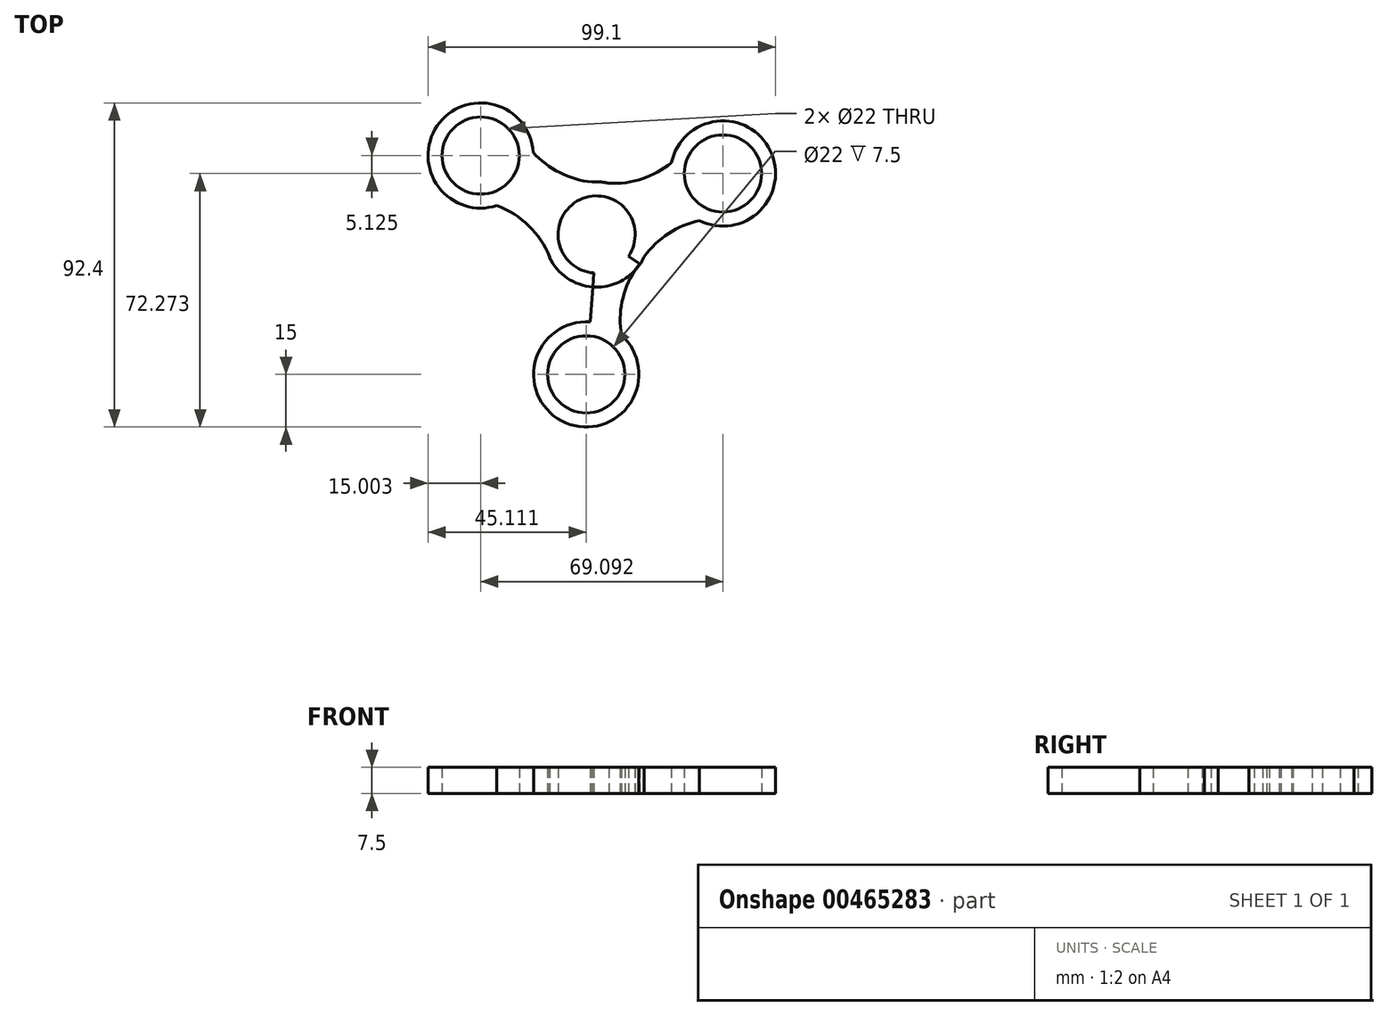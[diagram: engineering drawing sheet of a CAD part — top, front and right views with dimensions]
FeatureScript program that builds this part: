
annotation { "Feature Type Name" : "Feature", "Feature Type Description" : "" }
export const myFeature = defineFeature(function(context is Context, id is Id, definition is map)
    precondition{}
    {
        {
            var Q0;
            Q0=qCreatedBy(makeId("Top.planeOp"),FACE);
            var sketch = newSketch(context, id + "F0", { "sketchPlane" : qUnion([Q0])});
            skCircle(sketch, "E0", {"center": v(0, 0) * mm, "radius": 11 * mm});
            skCircle(sketch, "E1", {"center": v(0, 0) * mm, "radius": 15 * mm});
            skLineSegment(sketch, "E2", {"start": v(0, 0) * mm, "end": v(-33.07, 22.5) * mm});
            skLineSegment(sketch, "E3.1.0", {"start": v(0, 0) * mm, "end": v(-2.96, -39.9) * mm});
            skLineSegment(sketch, "E3.2.0", {"start": v(0, 0) * mm, "end": v(36.03, 17.38) * mm});
            skCircle(sketch, "E4", {"center": v(-33.07, 22.5) * mm, "radius": 11 * mm});
            skCircle(sketch, "E5", {"center": v(-33.07, 22.5) * mm, "radius": 15 * mm});
            skCircle(sketch, "E6", {"center": v(36.03, 17.38) * mm, "radius": 11 * mm});
            skCircle(sketch, "E7", {"center": v(36.03, 17.38) * mm, "radius": 15 * mm});
            skCircle(sketch, "E8", {"center": v(-2.96, -39.9) * mm, "radius": 11 * mm});
            skCircle(sketch, "E9", {"center": v(-2.96, -39.9) * mm, "radius": 15 * mm});
            skArc(sketch, "E10", {"start": v(0, 15) * mm, "mid": v(17.14, 17.67) * mm, "end": v(28.8, 30.52) * mm});
            skLineSegment(sketch, "E11", {"start": v(-2.96, -39.9) * mm, "end": v(3.85, 51.85) * mm});
            skLineSegment(sketch, "E12", {"start": v(-33.07, 22.5) * mm, "end": v(40.3, -27.44) * mm});
            skLineSegment(sketch, "E13", {"start": v(36.03, 17.38) * mm, "end": v(-52.53, -25.35) * mm});
            skArc(sketch, "E14.MirrorCS", {"start": v(2.21, 14.84) * mm, "mid": v(-14.35, 20) * mm, "end": v(-23.97, 34.44) * mm});
            skArc(sketch, "E15.MirrorCS", {"start": v(-13, -7.5) * mm, "mid": v(-23.87, 6.01) * mm, "end": v(-40.83, 9.67) * mm});
            skArc(sketch, "E16.MirrorCS", {"start": v(-13.95, -5.5) * mm, "mid": v(-10.15, -22.43) * mm, "end": v(-17.84, -37.98) * mm});
            skArc(sketch, "E17.MirrorCS", {"start": v(13, -7.5) * mm, "mid": v(6.73, -23.68) * mm, "end": v(12.04, -40.2) * mm});
            skArc(sketch, "E18.MirrorCS", {"start": v(11.74, -9.33) * mm, "mid": v(24.5, 2.43) * mm, "end": v(41.8, 3.54) * mm});
            skSolve(sketch);
        }
        {
            var Q0;
            {var subQ0=sQuery(id+"F0.wireOp",EDGE,"E14.MirrorCS");var subQ1=sQuery(id+"F0.wireOp",EDGE,"E1");var subQ2=makeQuery(id+"F0.imprint","INTERSECT",VERTEX,{"disambiguationData":[OD(1.0)],"derivedFrom":[subQ1,subQ0]});Q0=makeQuery(id+"F0.imprint","IMPRINT",FACE,{"disambiguationData":[TD([[makeQuery(id+"F0.imprint","IMPRINT",EDGE,{"disambiguationData":[TD([[subQ2,-1.0]])],"derivedFrom":subQ1}),-1.0]])]});}
            var Q1;
            {var subQ0=sQuery(id+"F0.wireOp",EDGE,"E13");var subQ1=sQuery(id+"F0.wireOp",EDGE,"E0");var subQ2=makeQuery(id+"F0.imprint","INTERSECT",VERTEX,{"disambiguationData":[OD(1.0)],"derivedFrom":[subQ1,subQ0]});Q1=makeQuery(id+"F0.imprint","IMPRINT",FACE,{"disambiguationData":[TD([[makeQuery(id+"F0.imprint","IMPRINT",EDGE,{"disambiguationData":[TD([[subQ2,-1.0]])],"derivedFrom":subQ1}),-1.0]])]});}
            var Q2;
            Q2=makeQuery(id+"F0.imprint","IMPRINT",FACE,{"disambiguationData":[TD([[makeQuery(id+"F0.imprint","IMPRINT",EDGE,{"derivedFrom":sQuery(id+"F0.wireOp",EDGE,"E4")}),-1.0]])]});
            var Q3;
            {var subQ0=sQuery(id+"F0.wireOp",EDGE,"E13");var subQ1=sQuery(id+"F0.wireOp",EDGE,"E0");var subQ2=makeQuery(id+"F0.imprint","INTERSECT",VERTEX,{"disambiguationData":[OD(0.0)],"derivedFrom":[subQ1,subQ0]});Q3=makeQuery(id+"F0.imprint","IMPRINT",FACE,{"disambiguationData":[TD([[makeQuery(id+"F0.imprint","IMPRINT",EDGE,{"disambiguationData":[TD([[subQ2,1.0]])],"derivedFrom":subQ1}),-1.0]])]});}
            var Q4;
            {var subQ0=sQuery(id+"F0.wireOp",EDGE,"E10");var subQ1=sQuery(id+"F0.wireOp",EDGE,"E7");var subQ2=makeQuery(id+"F0.imprint","INTERSECT",VERTEX,{"disambiguationData":[OD(0.0)],"derivedFrom":[subQ1,subQ0]});Q4=makeQuery(id+"F0.imprint","IMPRINT",FACE,{"disambiguationData":[TD([[makeQuery(id+"F0.imprint","IMPRINT",EDGE,{"disambiguationData":[TD([[subQ2,-1.0]])],"derivedFrom":subQ1}),1.0]])]});}
            var Q5;
            {var subQ0=sQuery(id+"F0.wireOp",EDGE,"E18.MirrorCS");var subQ1=sQuery(id+"F0.wireOp",EDGE,"E7");var subQ2=makeQuery(id+"F0.imprint","INTERSECT",VERTEX,{"disambiguationData":[OD(0.0)],"derivedFrom":[subQ1,subQ0]});Q5=makeQuery(id+"F0.imprint","IMPRINT",FACE,{"disambiguationData":[TD([[makeQuery(id+"F0.imprint","IMPRINT",EDGE,{"disambiguationData":[TD([[subQ2,1.0]])],"derivedFrom":subQ1}),1.0]])]});}
            var Q6;
            {var subQ0=sQuery(id+"F0.wireOp",EDGE,"E18.MirrorCS");var subQ1=sQuery(id+"F0.wireOp",EDGE,"E1");var subQ2=makeQuery(id+"F0.imprint","INTERSECT",VERTEX,{"disambiguationData":[OD(1.0)],"derivedFrom":[subQ1,subQ0]});Q6=makeQuery(id+"F0.imprint","IMPRINT",FACE,{"disambiguationData":[TD([[makeQuery(id+"F0.imprint","IMPRINT",EDGE,{"disambiguationData":[TD([[subQ2,-1.0]])],"derivedFrom":subQ1}),-1.0]])]});}
            var Q7;
            {var subQ1=sQuery(id+"F0.wireOp",EDGE,"E0");var subQ5=sQuery(id+"F0.wireOp",EDGE,"E11");var subQ6=makeQuery(id+"F0.imprint","INTERSECT",VERTEX,{"disambiguationData":[OD(1.0)],"derivedFrom":[subQ1,subQ5]});Q7=makeQuery(id+"F0.imprint","IMPRINT",FACE,{"disambiguationData":[TD([[makeQuery(id+"F0.imprint","IMPRINT",EDGE,{"disambiguationData":[TD([[subQ6,-1.0]])],"derivedFrom":subQ1}),-1.0]])]});}
            var Q8;
            {var subQ0=sQuery(id+"F0.wireOp",EDGE,"E16.MirrorCS");var subQ1=sQuery(id+"F0.wireOp",EDGE,"E1");var subQ2=makeQuery(id+"F0.imprint","INTERSECT",VERTEX,{"disambiguationData":[OD(1.0)],"derivedFrom":[subQ1,subQ0]});Q8=makeQuery(id+"F0.imprint","IMPRINT",FACE,{"disambiguationData":[TD([[makeQuery(id+"F0.imprint","IMPRINT",EDGE,{"disambiguationData":[TD([[subQ2,-1.0]])],"derivedFrom":subQ1}),-1.0]])]});}
            var Q9;
            {var subQ0=sQuery(id+"F0.wireOp",EDGE,"E10");var subQ1=sQuery(id+"F0.wireOp",EDGE,"E1");var subQ2=makeQuery(id+"F0.imprint","INTERSECT",VERTEX,{"disambiguationData":[OD(1.0)],"derivedFrom":[subQ1,subQ0]});Q9=makeQuery(id+"F0.imprint","IMPRINT",FACE,{"disambiguationData":[TD([[makeQuery(id+"F0.imprint","IMPRINT",EDGE,{"disambiguationData":[TD([[subQ2,1.0]])],"derivedFrom":subQ1}),-1.0]])]});}
            var Q10;
            {var subQ0=sQuery(id+"F0.wireOp",EDGE,"E17.MirrorCS");var subQ1=sQuery(id+"F0.wireOp",EDGE,"E9");var subQ2=makeQuery(id+"F0.imprint","INTERSECT",VERTEX,{"disambiguationData":[OD(0.0)],"derivedFrom":[subQ1,subQ0]});Q10=makeQuery(id+"F0.imprint","IMPRINT",FACE,{"disambiguationData":[TD([[makeQuery(id+"F0.imprint","IMPRINT",EDGE,{"disambiguationData":[TD([[subQ2,-1.0]])],"derivedFrom":subQ1}),1.0]])]});}
            var Q11;
            {var subQ0=sQuery(id+"F0.wireOp",EDGE,"E16.MirrorCS");var subQ1=sQuery(id+"F0.wireOp",EDGE,"E9");var subQ2=makeQuery(id+"F0.imprint","INTERSECT",VERTEX,{"disambiguationData":[OD(0.0)],"derivedFrom":[subQ1,subQ0]});Q11=makeQuery(id+"F0.imprint","IMPRINT",FACE,{"disambiguationData":[TD([[makeQuery(id+"F0.imprint","IMPRINT",EDGE,{"disambiguationData":[TD([[subQ2,1.0]])],"derivedFrom":subQ1}),1.0]])]});}
            var Q12;
            {var subQ0=sQuery(id+"F0.wireOp",EDGE,"E14.MirrorCS");var subQ1=sQuery(id+"F0.wireOp",EDGE,"E5");var subQ2=makeQuery(id+"F0.imprint","INTERSECT",VERTEX,{"disambiguationData":[OD(0.0)],"derivedFrom":[subQ1,subQ0]});Q12=makeQuery(id+"F0.imprint","IMPRINT",FACE,{"disambiguationData":[TD([[makeQuery(id+"F0.imprint","IMPRINT",EDGE,{"disambiguationData":[TD([[subQ2,1.0]])],"derivedFrom":subQ1}),1.0]])]});}
            var Q13;
            {var subQ0=sQuery(id+"F0.wireOp",EDGE,"E15.MirrorCS");var subQ1=sQuery(id+"F0.wireOp",EDGE,"E5");var subQ2=makeQuery(id+"F0.imprint","INTERSECT",VERTEX,{"disambiguationData":[OD(0.0)],"derivedFrom":[subQ1,subQ0]});Q13=makeQuery(id+"F0.imprint","IMPRINT",FACE,{"disambiguationData":[TD([[makeQuery(id+"F0.imprint","IMPRINT",EDGE,{"disambiguationData":[TD([[subQ2,-1.0]])],"derivedFrom":subQ1}),1.0]])]});}
            var Q14;
            {var subQ3=sQuery(id+"F0.wireOp",EDGE,"E11");var subQ7=sQuery(id+"F0.wireOp",EDGE,"E0");var subQ8=makeQuery(id+"F0.imprint","INTERSECT",VERTEX,{"disambiguationData":[OD(0.0)],"derivedFrom":[subQ7,subQ3]});Q14=makeQuery(id+"F0.imprint","IMPRINT",FACE,{"disambiguationData":[TD([[makeQuery(id+"F0.imprint","IMPRINT",EDGE,{"disambiguationData":[TD([[subQ8,1.0]])],"derivedFrom":subQ7}),-1.0]])]});}
            var Q15;
            {var subQ0=sQuery(id+"F0.wireOp",EDGE,"E15.MirrorCS");var subQ1=sQuery(id+"F0.wireOp",EDGE,"E1");var subQ2=makeQuery(id+"F0.imprint","INTERSECT",VERTEX,{"disambiguationData":[OD(1.0)],"derivedFrom":[subQ1,subQ0]});Q15=makeQuery(id+"F0.imprint","IMPRINT",FACE,{"disambiguationData":[TD([[makeQuery(id+"F0.imprint","IMPRINT",EDGE,{"disambiguationData":[TD([[subQ2,1.0]])],"derivedFrom":subQ1}),-1.0]])]});}
            var Q16;
            Q16=makeQuery(id+"F0.imprint","IMPRINT",FACE,{"disambiguationData":[TD([[makeQuery(id+"F0.imprint","IMPRINT",EDGE,{"derivedFrom":sQuery(id+"F0.wireOp",EDGE,"E6")}),-1.0]])]});
            var Q17;
            {var subQ0=sQuery(id+"F0.wireOp",EDGE,"E12");var subQ1=sQuery(id+"F0.wireOp",EDGE,"E0");var subQ2=makeQuery(id+"F0.imprint","INTERSECT",VERTEX,{"disambiguationData":[OD(0.0)],"derivedFrom":[subQ1,subQ0]});Q17=makeQuery(id+"F0.imprint","IMPRINT",FACE,{"disambiguationData":[TD([[makeQuery(id+"F0.imprint","IMPRINT",EDGE,{"disambiguationData":[TD([[subQ2,-1.0]])],"derivedFrom":subQ1}),-1.0]])]});}
            var Q18;
            {var subQ1=sQuery(id+"F0.wireOp",EDGE,"E0");var subQ5=sQuery(id+"F0.wireOp",EDGE,"E11");var subQ6=makeQuery(id+"F0.imprint","INTERSECT",VERTEX,{"disambiguationData":[OD(0.0)],"derivedFrom":[subQ1,subQ5]});Q18=makeQuery(id+"F0.imprint","IMPRINT",FACE,{"disambiguationData":[TD([[makeQuery(id+"F0.imprint","IMPRINT",EDGE,{"disambiguationData":[TD([[subQ6,-1.0]])],"derivedFrom":subQ1}),-1.0]])]});}
            var Q19;
            {var subQ0=sQuery(id+"F0.wireOp",EDGE,"E17.MirrorCS");var subQ1=sQuery(id+"F0.wireOp",EDGE,"E1");var subQ2=makeQuery(id+"F0.imprint","INTERSECT",VERTEX,{"disambiguationData":[OD(1.0)],"derivedFrom":[subQ1,subQ0]});Q19=makeQuery(id+"F0.imprint","IMPRINT",FACE,{"disambiguationData":[TD([[makeQuery(id+"F0.imprint","IMPRINT",EDGE,{"disambiguationData":[TD([[subQ2,1.0]])],"derivedFrom":subQ1}),-1.0]])]});}
            var Q20;
            Q20=makeQuery(id+"F0.imprint","IMPRINT",FACE,{"disambiguationData":[TD([[makeQuery(id+"F0.imprint","IMPRINT",EDGE,{"derivedFrom":sQuery(id+"F0.wireOp",EDGE,"E8")}),-1.0]])]});
            var Q21;
            {var subQ0=sQuery(id+"F0.wireOp",EDGE,"E10");var subQ1=sQuery(id+"F0.wireOp",EDGE,"E1");var subQ2=makeQuery(id+"F0.imprint","INTERSECT",VERTEX,{"disambiguationData":[OD(0.0)],"derivedFrom":[subQ1,subQ0]});Q21=makeQuery(id+"F0.imprint","IMPRINT",FACE,{"disambiguationData":[TD([[makeQuery(id+"F0.imprint","IMPRINT",EDGE,{"disambiguationData":[TD([[subQ2,1.0]])],"derivedFrom":subQ1}),1.0]])]});}
            var Q22;
            {var subQ0=sQuery(id+"F0.wireOp",EDGE,"E10");var subQ1=sQuery(id+"F0.wireOp",EDGE,"E1");var subQ2=makeQuery(id+"F0.imprint","INTERSECT",VERTEX,{"disambiguationData":[OD(0.0)],"derivedFrom":[subQ1,subQ0]});Q22=makeQuery(id+"F0.imprint","IMPRINT",FACE,{"disambiguationData":[TD([[makeQuery(id+"F0.imprint","IMPRINT",EDGE,{"disambiguationData":[TD([[subQ2,-1.0]])],"derivedFrom":subQ1}),1.0]])]});}
            var Q23;
            {var subQ0=sQuery(id+"F0.wireOp",EDGE,"E14.MirrorCS");var subQ1=sQuery(id+"F0.wireOp",EDGE,"E1");var subQ2=makeQuery(id+"F0.imprint","INTERSECT",VERTEX,{"disambiguationData":[OD(0.0)],"derivedFrom":[subQ1,subQ0]});Q23=makeQuery(id+"F0.imprint","IMPRINT",FACE,{"disambiguationData":[TD([[makeQuery(id+"F0.imprint","IMPRINT",EDGE,{"disambiguationData":[TD([[subQ2,1.0]])],"derivedFrom":subQ1}),1.0]])]});}
            var Q24;
            {var subQ0=sQuery(id+"F0.wireOp",EDGE,"E17.MirrorCS");var subQ1=sQuery(id+"F0.wireOp",EDGE,"E1");var subQ2=makeQuery(id+"F0.imprint","INTERSECT",VERTEX,{"disambiguationData":[OD(0.0)],"derivedFrom":[subQ1,subQ0]});Q24=makeQuery(id+"F0.imprint","IMPRINT",FACE,{"disambiguationData":[TD([[makeQuery(id+"F0.imprint","IMPRINT",EDGE,{"disambiguationData":[TD([[subQ2,-1.0]])],"derivedFrom":subQ1}),1.0]])]});}
            var Q25;
            {var subQ0=sQuery(id+"F0.wireOp",EDGE,"E18.MirrorCS");var subQ1=sQuery(id+"F0.wireOp",EDGE,"E1");var subQ2=makeQuery(id+"F0.imprint","INTERSECT",VERTEX,{"disambiguationData":[OD(0.0)],"derivedFrom":[subQ1,subQ0]});Q25=makeQuery(id+"F0.imprint","IMPRINT",FACE,{"disambiguationData":[TD([[makeQuery(id+"F0.imprint","IMPRINT",EDGE,{"disambiguationData":[TD([[subQ2,1.0]])],"derivedFrom":subQ1}),1.0]])]});}
            var Q26;
            {var subQ0=sQuery(id+"F0.wireOp",EDGE,"E15.MirrorCS");var subQ1=sQuery(id+"F0.wireOp",EDGE,"E1");var subQ2=makeQuery(id+"F0.imprint","INTERSECT",VERTEX,{"disambiguationData":[OD(0.0)],"derivedFrom":[subQ1,subQ0]});Q26=makeQuery(id+"F0.imprint","IMPRINT",FACE,{"disambiguationData":[TD([[makeQuery(id+"F0.imprint","IMPRINT",EDGE,{"disambiguationData":[TD([[subQ2,1.0]])],"derivedFrom":subQ1}),1.0]])]});}
            var Q27;
            {var subQ0=sQuery(id+"F0.wireOp",EDGE,"E16.MirrorCS");var subQ1=sQuery(id+"F0.wireOp",EDGE,"E1");var subQ2=makeQuery(id+"F0.imprint","INTERSECT",VERTEX,{"disambiguationData":[OD(0.0)],"derivedFrom":[subQ1,subQ0]});Q27=makeQuery(id+"F0.imprint","IMPRINT",FACE,{"disambiguationData":[TD([[makeQuery(id+"F0.imprint","IMPRINT",EDGE,{"disambiguationData":[TD([[subQ2,1.0]])],"derivedFrom":subQ1}),1.0]])]});}
            var Q28;
            {var subQ0=sQuery(id+"F0.wireOp",EDGE,"E15.MirrorCS");var subQ1=sQuery(id+"F0.wireOp",EDGE,"E1");var subQ2=makeQuery(id+"F0.imprint","INTERSECT",VERTEX,{"disambiguationData":[OD(0.0)],"derivedFrom":[subQ1,subQ0]});Q28=makeQuery(id+"F0.imprint","IMPRINT",FACE,{"disambiguationData":[TD([[makeQuery(id+"F0.imprint","IMPRINT",EDGE,{"disambiguationData":[TD([[subQ2,-1.0]])],"derivedFrom":subQ1}),1.0]])]});}
            var Q29;
            {var subQ0=sQuery(id+"F0.wireOp",EDGE,"E17.MirrorCS");var subQ1=sQuery(id+"F0.wireOp",EDGE,"E1");var subQ2=makeQuery(id+"F0.imprint","INTERSECT",VERTEX,{"disambiguationData":[OD(0.0)],"derivedFrom":[subQ1,subQ0]});Q29=makeQuery(id+"F0.imprint","IMPRINT",FACE,{"disambiguationData":[TD([[makeQuery(id+"F0.imprint","IMPRINT",EDGE,{"disambiguationData":[TD([[subQ2,1.0]])],"derivedFrom":subQ1}),1.0]])]});}
            var Q30;
            {var subQ0=sQuery(id+"F0.wireOp",EDGE,"E14.MirrorCS");var subQ1=sQuery(id+"F0.wireOp",EDGE,"E1");var subQ2=makeQuery(id+"F0.imprint","INTERSECT",VERTEX,{"disambiguationData":[OD(0.0)],"derivedFrom":[subQ1,subQ0]});Q30=makeQuery(id+"F0.imprint","IMPRINT",FACE,{"disambiguationData":[TD([[makeQuery(id+"F0.imprint","IMPRINT",EDGE,{"disambiguationData":[TD([[subQ2,-1.0]])],"derivedFrom":subQ1}),1.0]])]});}
            var Q31;
            {var subQ0=sQuery(id+"F0.wireOp",EDGE,"E16.MirrorCS");var subQ1=sQuery(id+"F0.wireOp",EDGE,"E1");var subQ2=makeQuery(id+"F0.imprint","INTERSECT",VERTEX,{"disambiguationData":[OD(0.0)],"derivedFrom":[subQ1,subQ0]});Q31=makeQuery(id+"F0.imprint","IMPRINT",FACE,{"disambiguationData":[TD([[makeQuery(id+"F0.imprint","IMPRINT",EDGE,{"disambiguationData":[TD([[subQ2,-1.0]])],"derivedFrom":subQ1}),1.0]])]});}
            var Q32;
            {var subQ0=sQuery(id+"F0.wireOp",EDGE,"E18.MirrorCS");var subQ1=sQuery(id+"F0.wireOp",EDGE,"E1");var subQ2=makeQuery(id+"F0.imprint","INTERSECT",VERTEX,{"disambiguationData":[OD(0.0)],"derivedFrom":[subQ1,subQ0]});Q32=makeQuery(id+"F0.imprint","IMPRINT",FACE,{"disambiguationData":[TD([[makeQuery(id+"F0.imprint","IMPRINT",EDGE,{"disambiguationData":[TD([[subQ2,-1.0]])],"derivedFrom":subQ1}),1.0]])]});}
            extrude(context, id + "F1", {"entities" : qUnion([Q0, Q1, Q2, Q3, Q4, Q5, Q6, Q7, Q8, Q9, Q10, Q11, Q12, Q13, Q14, Q15, Q16, Q17, Q18, Q19, Q20, Q21, Q22, Q23, Q24, Q25, Q26, Q27, Q28, Q29, Q30, Q31, Q32]), "depth" : 7.5 * mm});
        }
    });
